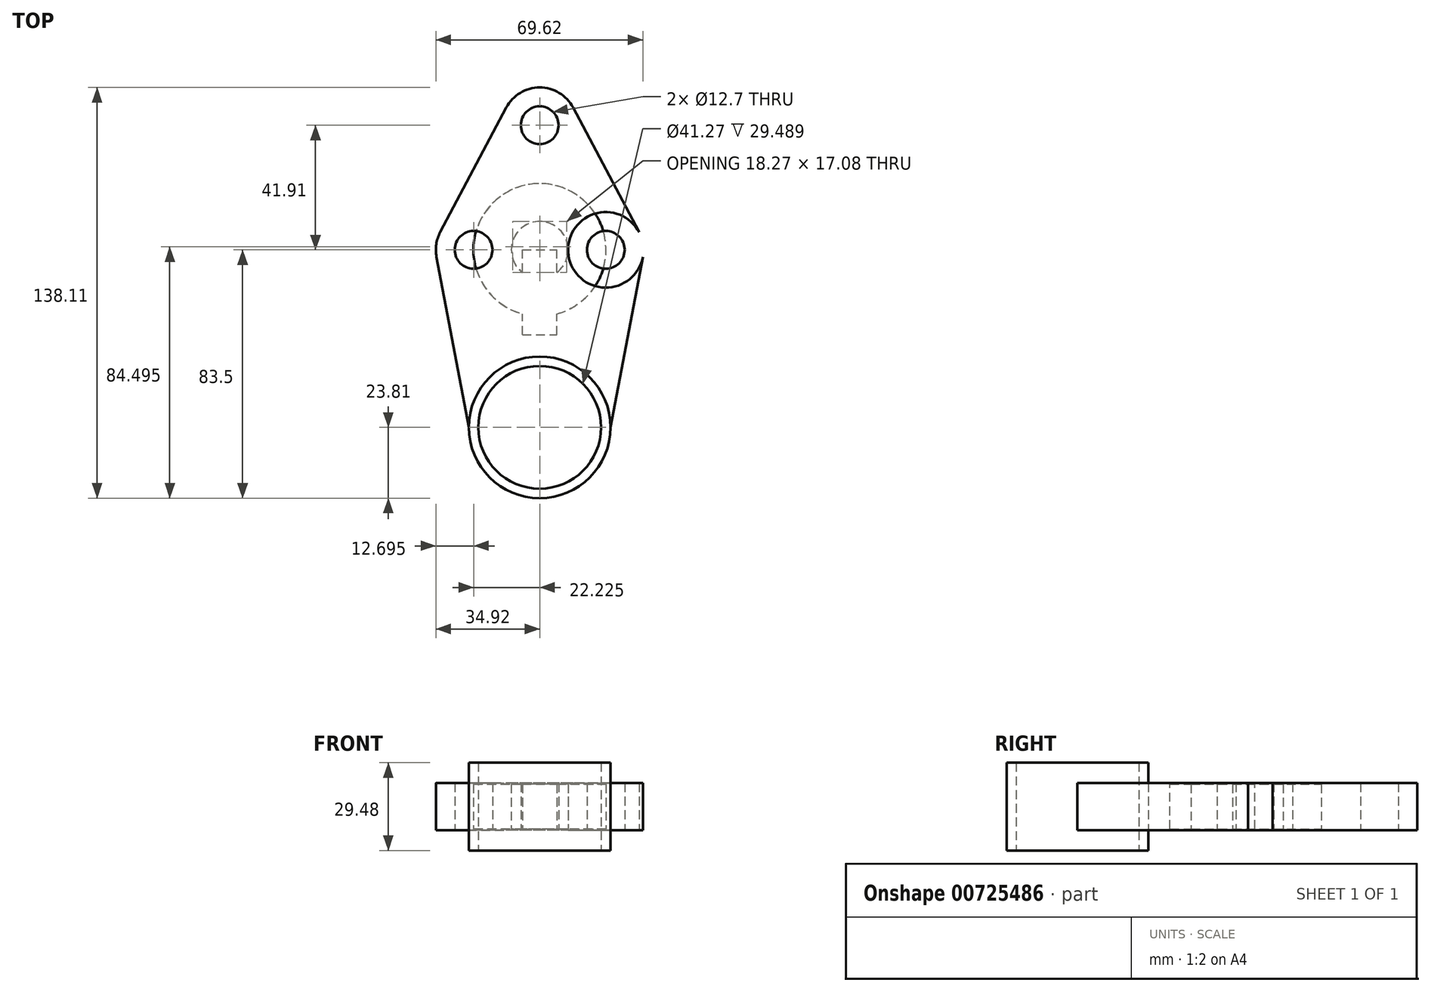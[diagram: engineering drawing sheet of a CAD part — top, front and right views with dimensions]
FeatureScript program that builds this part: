
annotation { "Feature Type Name" : "Feature", "Feature Type Description" : "" }
export const myFeature = defineFeature(function(context is Context, id is Id, definition is map)
    precondition{}
    {
        {
            var Q0;
            Q0=qCreatedBy(makeId("Top.planeOp"),FACE);
            var sketch = newSketch(context, id + "F0", { "sketchPlane" : qUnion([Q0])});
            skCircle(sketch, "E0", {"center": v(0, 0) * mm, "radius": 9.54 * mm});
            skCircle(sketch, "E1", {"center": v(0, 0) * mm, "radius": 22.29 * mm});
            skSolve(sketch);
        }
        {
            var Q0;
            Q0=makeQuery(id+"F0.imprint","IMPRINT",FACE,{"disambiguationData":[TD([[makeQuery(id+"F0.imprint","IMPRINT",EDGE,{"derivedFrom":sQuery(id+"F0.wireOp",EDGE,"E0")}),-1.0]])]});
            extrude(context, id + "F1", {"entities" : qUnion([Q0]), "depth" : 15.06 * mm, "offsetDistance" : 25.4 * mm, "symmetric" : true});
        }
        {
            var Q0;
            Q0=qCreatedBy(makeId("Front.planeOp"),FACE);
            var sketch = newSketch(context, id + "F2", { "sketchPlane" : qUnion([Q0])});
            skCircle(sketch, "E2", {"center": v(0, 0) * mm, "radius": 9.53 * mm});
            skSolve(sketch);
        }
        {
            var Q0;
            Q0=qCreatedBy(makeId("Front.planeOp"),FACE);
            var sketch = newSketch(context, id + "F3", { "sketchPlane" : qUnion([Q0])});
            skPoint(sketch, "E3.0", {"position": v(-5.83, 7.53) * mm});
            skPoint(sketch, "E4.0", {"position": v(5.83, 7.53) * mm});
            skPoint(sketch, "E5.0", {"position": v(5.83, -7.53) * mm});
            skPoint(sketch, "E6.0", {"position": v(-5.83, -7.53) * mm});
            skLineSegment(sketch, "E7.bottom", {"start": v(-5.83, -7.53) * mm, "end": v(5.83, -7.53) * mm});
            skLineSegment(sketch, "E7.top", {"start": v(-5.83, 7.53) * mm, "end": v(5.83, 7.53) * mm});
            skLineSegment(sketch, "E7.left", {"start": v(-5.83, -7.53) * mm, "end": v(-5.83, 7.53) * mm});
            skLineSegment(sketch, "E7.right", {"start": v(5.83, -7.53) * mm, "end": v(5.83, 7.53) * mm});
            skLineSegment(sketch, "E8", {"start": v(0, 0) * mm, "end": v(-22.29, 0) * mm});
            skLineSegment(sketch, "E9", {"start": v(0, 0) * mm, "end": v(22.29, 0) * mm});
            skSolve(sketch);
        }
        {
            var Q0;
            Q0=makeQuery(id+"F3.imprint","IMPRINT",FACE,{"disambiguationData":[TD([[makeQuery(id+"F3.imprint","IMPRINT",EDGE,{"derivedFrom":sQuery(id+"F3.wireOp",EDGE,"E7.bottom")}),1.0]])]});
            var Q1;
            {var subQ1=sQuery(id+"F3.wireOp",EDGE,"E7.top");Q1=makeQuery(id+"F3.imprint","IMPRINT",FACE,{"disambiguationData":[TD([[makeQuery(id+"F3.imprint","IMPRINT",EDGE,{"derivedFrom":subQ1}),-1.0]])]});}
            extrude(context, id + "F4", {"entities" : qUnion([Q0, Q1]), "operationType" : NewBodyOperationType.ADD, "depth" : 28.57 * mm, "offsetDistance" : 25.4 * mm});
        }
        {
            var Q0;
            Q0=qCreatedBy(makeId("Top.planeOp"),FACE);
            var sketch = newSketch(context, id + "F5", { "sketchPlane" : qUnion([Q0])});
            skLineSegment(sketch, "E10", {"start": v(0, 0) * mm, "end": v(28.58, 0) * mm, "construction": true});
            skLineSegment(sketch, "E11", {"start": v(0, 0) * mm, "end": v(-28.58, 0) * mm, "construction": true});
            skLineSegment(sketch, "E12", {"start": v(-28.58, 0) * mm, "end": v(-22.23, 0) * mm, "construction": true});
            skCircle(sketch, "E13", {"center": v(-22.23, 0) * mm, "radius": 6.35 * mm});
            skCircle(sketch, "E14.MirrorC", {"center": v(22.23, 0) * mm, "radius": 6.35 * mm});
            skCircle(sketch, "E15", {"center": v(0, 41.91) * mm, "radius": 6.35 * mm});
            skLineSegment(sketch, "E16", {"start": v(0, 41.91) * mm, "end": v(0, -59.7) * mm, "construction": true});
            skCircle(sketch, "E17", {"center": v(0, -59.7) * mm, "radius": 23.81 * mm});
            skCircle(sketch, "E18", {"center": v(0, -59.7) * mm, "radius": 20.64 * mm});
            skLineSegment(sketch, "E19", {"start": v(28.58, 0) * mm, "end": v(34.93, 0) * mm, "construction": true});
            skLineSegment(sketch, "E20", {"start": v(-28.58, 0) * mm, "end": v(-34.93, 0) * mm, "construction": true});
            skLineSegment(sketch, "E21", {"start": v(0, 48.26) * mm, "end": v(0, 54.61) * mm, "construction": true});
            skLineSegment(sketch, "E22", {"start": v(0, -59.7) * mm, "end": v(34.93, 0) * mm, "construction": true});
            skLineSegment(sketch, "E23", {"start": v(0, -59.7) * mm, "end": v(-34.93, 0) * mm, "construction": true});
            skCircle(sketch, "E24", {"center": v(0, 41.91) * mm, "radius": 12.7 * mm});
            skCircle(sketch, "E25", {"center": v(-22.23, 0) * mm, "radius": 12.7 * mm});
            skCircle(sketch, "E26", {"center": v(22.23, 0) * mm, "radius": 12.7 * mm});
            skLineSegment(sketch, "E27", {"start": v(0, -59.7) * mm, "end": v(-23.81, -59.7) * mm, "construction": true});
            skLineSegment(sketch, "E28", {"start": v(0, -59.7) * mm, "end": v(23.81, -59.7) * mm, "construction": true});
            skLineSegment(sketch, "E29", {"start": v(-23.81, -59.69) * mm, "end": v(-34.7, -2.37) * mm});
            skLineSegment(sketch, "E30", {"start": v(23.81, -59.7) * mm, "end": v(34.7, -2.37) * mm});
            skLineSegment(sketch, "E31", {"start": v(-33.44, 5.95) * mm, "end": v(-11.22, 47.86) * mm});
            skLineSegment(sketch, "E32", {"start": v(11.22, 47.86) * mm, "end": v(33.44, 5.95) * mm});
            skSolve(sketch);
        }
        {
            var Q0;
            {var subQ3=sQuery(id+"F5.wireOp",EDGE,"E29");Q0=makeQuery(id+"F5.imprint","IMPRINT",FACE,{"disambiguationData":[TD([[makeQuery(id+"F5.imprint","IMPRINT",EDGE,{"derivedFrom":subQ3}),-1.0]])]});}
            var Q1;
            Q1=makeQuery(id+"F5.imprint","IMPRINT",FACE,{"disambiguationData":[TD([[makeQuery(id+"F5.imprint","IMPRINT",EDGE,{"derivedFrom":sQuery(id+"F5.wireOp",EDGE,"E13")}),-1.0]])]});
            var Q2;
            Q2=makeQuery(id+"F5.imprint","IMPRINT",FACE,{"disambiguationData":[TD([[makeQuery(id+"F5.imprint","IMPRINT",EDGE,{"derivedFrom":sQuery(id+"F5.wireOp",EDGE,"E14.MirrorC")}),1.0]])]});
            var Q3;
            Q3=makeQuery(id+"F5.imprint","IMPRINT",FACE,{"disambiguationData":[TD([[makeQuery(id+"F5.imprint","IMPRINT",EDGE,{"derivedFrom":sQuery(id+"F5.wireOp",EDGE,"E15")}),-1.0]])]});
            extrude(context, id + "F6", {"entities" : qUnion([Q0, Q1, Q2, Q3]), "depth" : 15.88 * mm, "offsetDistance" : 25.4 * mm, "symmetric" : true});
        }
        {
            var Q0;
            Q0=makeQuery(id+"F5.imprint","IMPRINT",FACE,{"disambiguationData":[TD([[makeQuery(id+"F5.imprint","IMPRINT",EDGE,{"derivedFrom":sQuery(id+"F5.wireOp",EDGE,"E18")}),-1.0]])]});
            extrude(context, id + "F7", {"entities" : qUnion([Q0]), "depth" : 29.49 * mm, "offsetDistance" : 25.4 * mm, "symmetric" : true});
        }
    });
